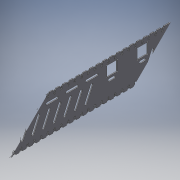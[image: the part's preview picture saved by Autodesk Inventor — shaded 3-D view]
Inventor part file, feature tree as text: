
AUTODESK INVENTOR PART (.ipt)
format: ipt  version: 2016 (Build 200138000, 138)  size: 936,448 bytes
history: native  units: in
note: dims shown in document units (in); Inventor stores cm internally (conversion verified against a paired STEP export)
features: extrude x14, sketch x14, pattern_linear x6, mirror x2, projected_geometry x1
ambient origin geometry x8: Origin, YZ Plane, XZ Plane, XY Plane, X Axis, Y Axis, Z Axis, Center Point
bodies: Solid1 (feature_tree)
feature tree (37):
  extrude  "Extrusion1"  Depth=5.5118in
  extrude  "Extrusion2"  Depth=0.125in
  extrude  "Extrusion3"  Depth=0.5in
  extrude  "Extrusion4"  Depth=0.2362in
  extrude  "Extrusion5"  Depth=0.18in
  pattern_linear  "Rectangular Pattern1"  Count1=23 Spacing1=1.0in
  extrude  "Extrusion6"  Depth=0.125in
  extrude  "Extrusion7"  Depth=0.5in
  extrude  "Extrusion8"  Depth=0.625in
  extrude  "Extrusion9"  Depth=0.3937in TaperAngle=0.0deg
  pattern_linear  "Rectangular Pattern2"  Spacing1=0.2362in  [1 undecoded]
  mirror  "Mirror1"
  extrude  "Extrusion10"  Depth=0.14in
  pattern_linear  "Rectangular Pattern3"  Spacing1=0.18in  [1 undecoded]
  sketch  "Sketch11"  dims[d18=0.25in d19=0.0in]
  pattern_linear  "Rectangular Pattern4"  Spacing1=0.25in  [1 undecoded]
  pattern_linear  "Rectangular Pattern5"  Spacing1=0.1094in  [1 undecoded]
  mirror  "Mirror2"
  extrude  "Extrusion12"  Depth=0.3125in
  extrude  "Extrusion13"  TaperAngle=0.0deg  [1 undecoded]
  extrude  "Extrusion14"  Depth=0.0937in
  pattern_linear  "Rectangular Pattern10"  Spacing1=0.25in  [1 undecoded]
  extrude  "Extrusion15"  Depth=0.1404in
  sketch  "Sketch1"  dims[d0=24.125in d1=5.5118in]
  sketch  "Sketch2"  dims[d2=0.125in d3=0.0in d4=0.125in]
  sketch  "Sketch3"  dims[d5=0.5in d6=0.5in]
  sketch  "Sketch4"  dims[d7=0.25in d8=0.0in d9=0.2362in]
  sketch  "Sketch5"  dims[d10=0.14in d11=0.18in]
  sketch  "Sketch6"  dims[d12=0.25in d13=0.0in]
  sketch  "Sketch7"  dims[d14=0.1094in]
  sketch  "Sketch8"  dims[d15=0.3125in]
  sketch  "Sketch9"  dims[d16=0.0in]
  sketch  "Sketch10"  dims[d17=0.0937in]
  projected_geometry  "Projected Loop1"
  sketch  "Sketch12"  dims[d20=0.1404in]
  sketch  "Sketch13"  dims[d22=0.0863in]
  sketch  "Sketch14"  dims[d23=0.25in d24=0.0in d25=9.0551in d27=1.0in d28=0.125in d29=0.5in d30=0.625in d31=0.25in d32=0.0in d33=0.2362in d34=0.14in d35=0.18in d36=0.25in d37=0.0in d38=0.1094in d39=0.3125in d40=0.0in d41=0.0937in d42=0.25in d43=0.0in d44=0.1404in d46=0.0863in d47=0.25in d48=0.0in d49=1.9685in d51=1.0in d52=1.9685in d53=1.378in d54=0.25in d55=0.0in d56=2.7559in d58=1.5748in d59=1.9335in d60=0.3816in d61=0.6in d62=0.6in d67=0.7874in d69=18.5039in d70=0.7874in d72=19.2913in d75=0.1693in d76=0.1693in d77=0.1693in d78=0.1693in d82=3.5433in d85=3.1496in d86=1.5748in d87=1.5748in d88=1.5748in d89=1.5748in d90=0.0197in d91=0.0197in d92=0.0197in d93=0.0197in d94=0.3937in d95=0.0in d96=0.1693in d97=0.1693in d98=0.1693in d99=0.1693in d100=1.5748in d101=1.5748in d102=1.5748in d103=1.5748in d106=2.9528in d107=0.0197in d108=0.0197in d109=0.0197in d110=0.0197in d111=0.3937in d112=0.0in d125=0.18in d126=0.3937in d127=0.0in d128=1.5748in d130=2.9528in d131=0.3937in d132=0.0in]
note: 6 required parameter values undecoded (feature->parameter linkage not recoverable at this tier; creation-order binding heuristic only, values carry confidence <= 0.55)
